# Revit family: ДВО-02 30 Вт 595
name_source: partatom
category: Осветительные приборы
units: mm (PartAtom-declared; Revit-internal decimal feet)

## family parameters
Всегда вертикально = Да
Заголовок OmniClass = Luminaries for Internal Lighting
Источник света = Да
Номер OmniClass = 23.80.70.11
Общий = Нет
Основа = Потолок
При загрузке вырезать с полостями = Нет
Размер круглого соединителя = Использовать диаметр
Тип детали = Нормальный
Точка расчета площади = Нет

## types (3) — shared parameters
ADSK_Размер_Высота = 45 мм
ADSK_Размер_Длина = 595 мм
ADSK_Размер_Ширина = 595 мм
URL = http://innolux.pro
Блок аварийного питания = нет
Бренд светодиодов = EDISON
Вес светильника = 2.9 кг
Время импульса пускового тока = 200 мс
Гарантия = 7 лет
Диммирование = нет
Изготовитель = INNOLUX
Индекс цветопередачи = >80
Категория по ограничению яркости = 1
Класс защиты от поражения током = I
Класс светораспределения по ГОСТ 54350-2011 = П
Климатическое исполнение = УХЛ 4
Кол-во светодиодов = 180
Количество в упаковке = 4
Количество модулей = 10
Коэффициент мощности = >0.95
>0.95
>0.95
Коэффициент пульсации = <5%
Материал корпуса = Металл, окрашенный, белый, матовый
Материал рассеивателя = Полистирол
Напряжение = 176-264 В
Объём упаковки = 0.22*0.61*0.61 м
Полная установленная мощность = 30 В·А
Потребляемый ток = 0
Пусковой ток = 26 А
Световой поток модуля = 500
Светофильтр = 16777215
Сила тока = 0.14 А
Смещение цветовой температуры при затухании лампы = <Нет>
Способ монтажа = Встраиваемый / Накладной
Срок службы = 80000
Степень защиты (IP) = 40
Тип кривой силы света по ГОСТ 54350-2011 = Д
Тип рассеивателя = опал
Типоразмер светодиода = 2835
Угол наклона = 90.00°
Цвет корпуса = Белый
Частота сети = 50 / 60 Гц
Эффективность светильника = 123

## per-type parameters (varying)
| type | Артикул | Габаритная яркость | Диапазон рабочих температур | Файл фотометрической сетки |
| ДВО-02-О-30-3К-IP40-Армстронг | 14766 | <5000 кд / м14 | - 20 + 40°C | INNOLUX 14 766 DVO-02-O-30-3K-IP40.ies |
| ДВО-02-О-30-4К-IP40-Армстронг | 14768 | <5000 кд / м16 | - 20 + 40°C | INNOLUX 14 768 DVO-02-O-30-4K-IP40.ies |
| ДВО-02-О-30-5К-IP40-Армстронг | 14770 | <5000 кд / м18 | -20 + 40°C | INNOLUX 14 770 DVO-02-O-30-5K-IP40.ies |
